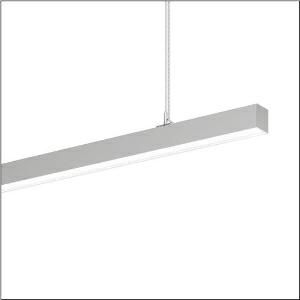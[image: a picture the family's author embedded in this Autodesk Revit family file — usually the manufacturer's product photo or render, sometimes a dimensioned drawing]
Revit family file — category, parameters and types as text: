
# Revit family: silica_r__21_51mx30tct9s_9c67
name_source: partatom
category: Lighting Fixtures
units: mm (PartAtom-declared; Revit-internal decimal feet)

## family parameters
Cut with Voids When Loaded = No
Host = Face
Light Source = No
Part Type = Normal
Room Calculation Point = No
Round Connector Dimension = Use Diameter
Shared = No

## types (1)
- --- (1 x LED, 10300 lm, 84.4 W, 6500K)
    Apparent Load = 84 VA
    CIE Flux Codes = 47 79 96 58 100
    Color Rendering = 80
    Color Temperature = 6500K
    Default Elevation = 1800 mm
    Description = Silica® 21, office luminaire, primary optical cover: cover, of PMMA, opal, light emission: direct/indirect distribution, primary light characteristic: symmetric, installation type: suspended mounting, LED, rated luminous flux: 10.300lm, luminous efficacy: 116lm/W, light colour: 8tw, colour temperature: 2700..6500K, control gear: ECG DALI, with terminal, 3+2-pole, max. 2.5mm², mains connection: 220..240V, AC, 50/60Hz, rated input power: 88.7W, luminaire housing, of aluminium, metallic grey (RAL 9006), length: 3.004mm, width: 53mm, height: 53mm, protection rating (complete): IP20, insulation class (complete): insulation class I (protective earthing), certification: CE, permissible operating ambient temperature: 0..+35°C, standard: EN 50419, packaging unit: 1 piece
    Height = 53 mm
    Lamp = 1 x LED
    Lamp Light Flux = 10300 lm
    Lamp Power = 84.4 W
    Lamp count = 1
    Length = 3004 mm
    Luminous efficacy = 122 lm/W
    Manufacturer = Siteco
    ModVariant = No
    Model = 51MX30TCT9S
    Mounting Place = Ceiling
    Mounting Type = Pendant
    Number of Poles = 1
    OnlyDefault = Yes
    Power Factor = 1
    Product Name = Silica® 21
    Product group = office luminaire | ceiling pendant
    ProductGroupID = 902
    Protection Class = Protection class I
    Protection Degree = IP 20
    RLX_Detail_Level = 1
    RLX_Emergency_Light_Flux = 0 lm
    RLX_Emergency_Type = 0
    RLX_Emergency_Type_DB = No
    RlxData = <blob elided: 20057 chars, md5=45a70350>
    Socket = socket
    Standby Power = 0 W
    System Light Flux = 10300 lm
    System Power = 84 W
    Type Comments = individual setting
    Type Image = l_1335864.jpg
    URL = http://relux.com
    VarID = @adj_109411
    Voltage = 0 V
    Weight = 0.00 kg
    Width = 53 mm

## geometry (parser evidence)
native form markers: Blend x4, Sweep x12
no freeform markers — native parametric forms only
